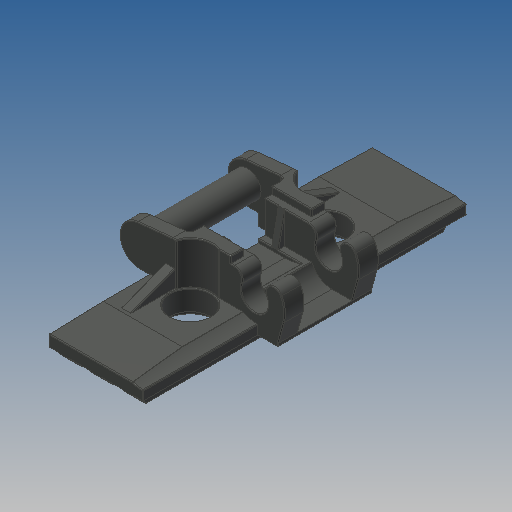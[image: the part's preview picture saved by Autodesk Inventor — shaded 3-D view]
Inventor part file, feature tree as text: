
AUTODESK INVENTOR PART (.ipt)
format: ipt  version: 2022.2 (Build 262287010, 287A)  size: 954,368 bytes
history: native  units: in
note: dims shown in document units (in); Inventor stores cm internally (conversion verified against a paired STEP export)
features: extrude x15, sketch x9, fillet x3, plane x2, revolve x1
ambient origin geometry x8: Origin, YZ Plane, XZ Plane, XY Plane, X Axis, Y Axis, Z Axis, Center Point
bodies: Solid2 (feature_tree)
feature tree (30):
  sketch  "Sketch2"  dims[d0=0.126in d1=0.4724in]
  extrude  "Extrusion5"  Depth=0.4724in
  extrude  "Extrusion10"  Depth=0.4409in
  extrude  "Extrusion2"  Depth=0.0472in
  extrude  "Extrusion4"  Depth=0.2362in
  extrude  "Extrusion6"  Depth=0.0945in
  extrude  "Extrusion7"  Depth=0.0315in
  extrude  "Extrusion9"  Depth=0.1102in
  extrude  "Extrusion8"  Depth=0.189in
  fillet  "Fillet1"  Radius=0.0945in
  sketch  "Sketch6"  dims[d6=0.2835in d7=0.2362in]
  extrude  "Extrusion11"  Depth=0.0039in TaperAngle=0.0deg
  extrude  "Extrusion12"  Depth=0.0039in TaperAngle=0.0deg
  extrude  "Extrusion13"  Depth=0.0039in TaperAngle=0.0deg
  sketch  "Sketch8"  dims[d12=0.1732in d14=0.0315in]
  extrude  "Extrusion14"  Depth=0.0039in TaperAngle=0.0deg
  extrude  "Extrusion15"  Depth=0.0039in
  revolve  "Revolution1"  [1 undecoded]
  plane  "Work Plane1"
  extrude  "Extrusion16"  Depth=0.0039in
  plane  "Work Plane2"
  extrude  "Extrusion17"  Depth=0.0039in
  fillet  "Fillet2"  Radius=0.189in
  fillet  "Fillet3"  Radius=0.315in
  sketch  "Sketch3"  dims[d2=0.189in d3=0.4409in]
  sketch  "Sketch5"  dims[d4=0.0551in d5=0.0472in]
  sketch  "Sketch7"  dims[d8=0.0157in d9=0.0945in]
  sketch  "Sketch9"  dims[d15=0.2087in d16=0.1102in]
  sketch  "Sketch10"  dims[d19=0.063in d20=0.189in d21=0.0945in]
  sketch  "Sketch11"  dims[d22=0.0157in d25=1.5118in d26=0.0in d29=0.1732in d30=0.4409in d31=0.0in d32=0.5669in d33=0.0in d34=0.252in d35=0.0in d36=0.1732in d37=0.189in d38=0.0in d39=0.2047in d40=0.126in d42=0.189in d43=0.0in d44=0.315in d45=0.0in d51=0.4409in d52=0.1906in d53=0.0551in d54=0.0079in d55=0.315in d56=0.0in d57=0.0197in d58=0.2835in d59=0.6299in d60=0.2205in d61=0.252in d62=0.189in d63=0.1024in d64=0.1024in d65=0.0472in d66=0.0472in d67=0.0472in d68=0.189in d69=0.063in d70=0.0in d71=0.063in d72=0.0in d73=0.0315in d74=0.0in d75=0.2741in d76=0.0315in d77=0.0in d78=0.0315in d79=0.0in d80=0.252in d81=0.0551in d82=0.0687in d83=0.0157in d84=0.189in d85=0.1575in d86=0.0157in d87=0.0157in d88=90.0deg d89=-0.0709in d90=0.0787in d91=0.2047in d92=0.0472in d93=0.0in d94=-0.189in d95=0.0315in d96=0.0in d97=0.0039in d98=0.0039in d99=0.0in d100=0.0in]
note: 1 required parameter value undecoded (feature->parameter linkage not recoverable at this tier; creation-order binding heuristic only, values carry confidence <= 0.55)
